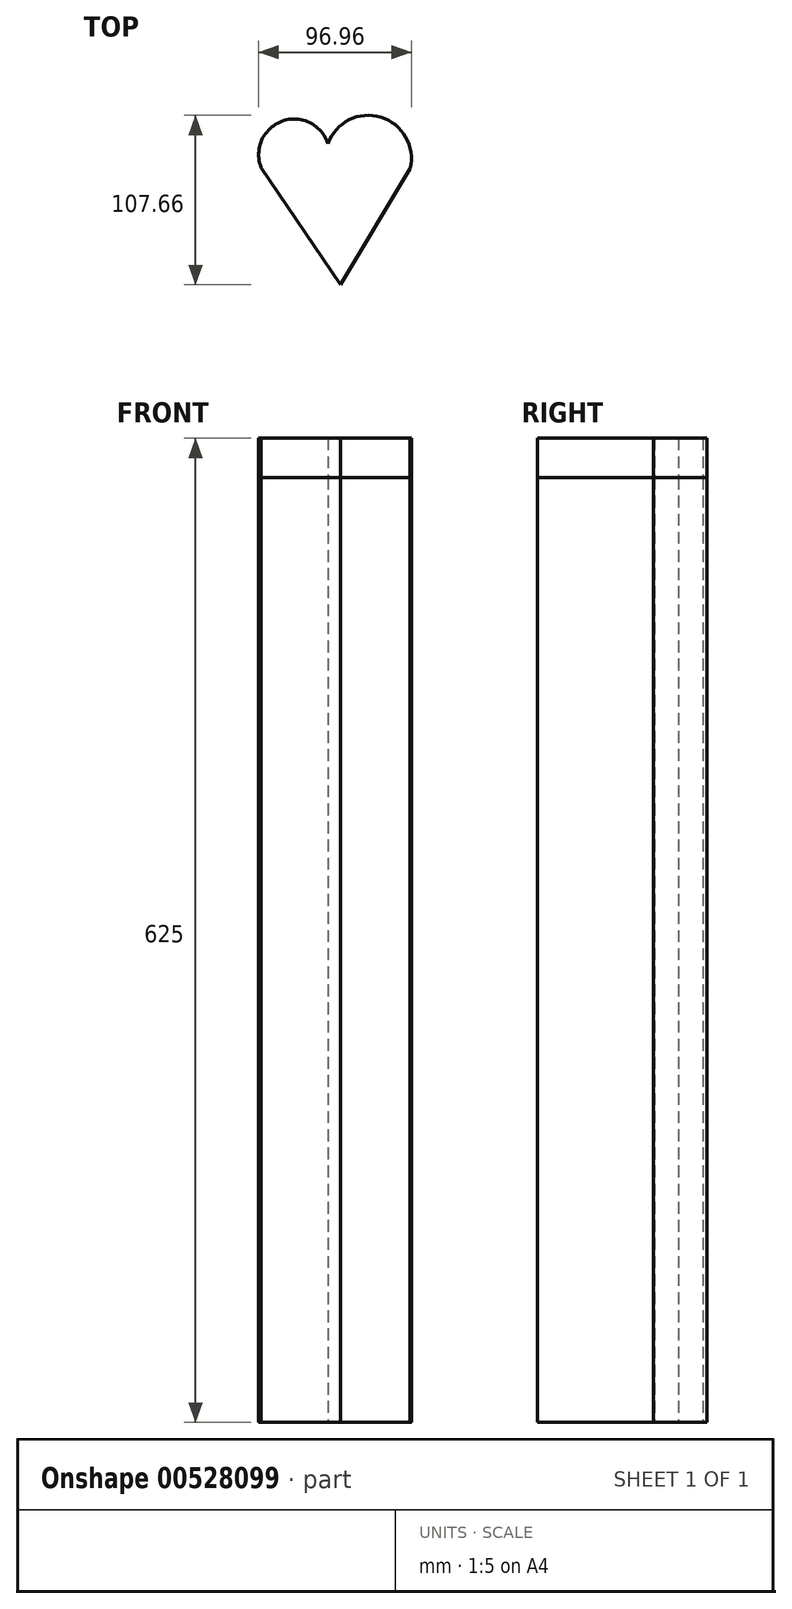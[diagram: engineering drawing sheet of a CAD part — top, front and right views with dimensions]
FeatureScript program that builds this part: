
annotation { "Feature Type Name" : "Feature", "Feature Type Description" : "" }
export const myFeature = defineFeature(function(context is Context, id is Id, definition is map)
    precondition{}
    {
        {
            var Q0;
            Q0=qCreatedBy(makeId("Top.planeOp"),FACE);
            var sketch = newSketch(context, id + "F0", { "sketchPlane" : qUnion([Q0])});
            skLineSegment(sketch, "E0", {"start": v(-57.7, 15.3) * mm, "end": v(-7.29, -59.08) * mm});
            skLineSegment(sketch, "E1", {"start": v(-7.29, -59.08) * mm, "end": v(36.83, 14.66) * mm});
            skArc(sketch, "E2", {"start": v(36.83, 14.66) * mm, "mid": v(10.36, 48.58) * mm, "end": v(-16.1, 14.66) * mm});
            skArc(sketch, "E3", {"start": v(-16.1, 14.66) * mm, "mid": v(-36.44, 46.18) * mm, "end": v(-57.7, 15.3) * mm});
            skSolve(sketch);
        }
        {
            var Q0;
            Q0 = qSketchRegion(id + "F0", true);
            extrude(context, id + "F1", {"entities" : qUnion([Q0]), "depth" : 600 * mm, "offsetDistance" : 25 * mm});
        }
        {
            var Q0;
            Q0=makeQuery(id+"F1.opExtrude","CAP_FACE",FACE,{"disambiguationData":[OSD([sQuery(id+"F0.wireOp",EDGE,"E0"),sQuery(id+"F0.wireOp",EDGE,"E1"),sQuery(id+"F0.wireOp",EDGE,"E2"),sQuery(id+"F0.wireOp",EDGE,"E3")])],"isStart":false});
            var sketch = newSketch(context, id + "F2", { "sketchPlane" : qUnion([Q0])});
            skSolve(sketch);
        }
        {
            var Q0;
            Q0=makeQuery(id+"F2.imprint","IMPRINT",FACE,{"disambiguationData":[TD([[makeQuery(id+"F2.imprint","IMPRINT",EDGE,{"derivedFrom":makeQuery(id+"F1.opExtrude","CAP_EDGE",EDGE,{"disambiguationData":[OSD([sQuery(id+"F0.wireOp",EDGE,"E0")])],"isStart":false})}),1.0]])]});
            extrude(context, id + "F3", {"entities" : qUnion([Q0]), "depth" : 25 * mm, "offsetDistance" : 25 * mm});
        }
    });
